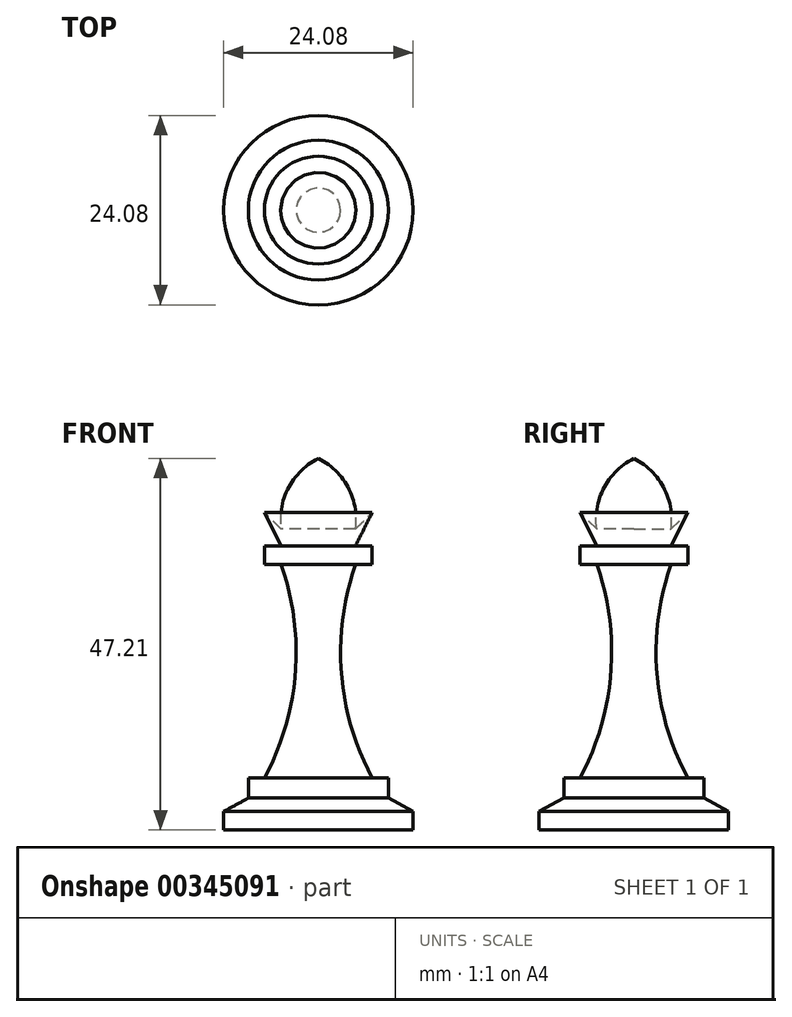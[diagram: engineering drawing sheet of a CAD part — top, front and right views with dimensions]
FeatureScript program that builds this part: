
annotation { "Feature Type Name" : "Feature", "Feature Type Description" : "" }
export const myFeature = defineFeature(function(context is Context, id is Id, definition is map)
    precondition{}
    {
        {
            var Q0;
            Q0=qCreatedBy(makeId("Front.planeOp"),FACE);
            var sketch = newSketch(context, id + "F0", { "sketchPlane" : qUnion([Q0])});
            skLineSegment(sketch, "E0", {"start": v(4.72, 27.14) * mm, "end": v(6.84, 27.14) * mm});
            skLineSegment(sketch, "E1", {"start": v(6.84, 27.14) * mm, "end": v(6.84, 29.5) * mm});
            skLineSegment(sketch, "E2", {"start": v(6.84, 29.5) * mm, "end": v(4.72, 29.5) * mm});
            skLineSegment(sketch, "E3", {"start": v(4.72, 29.5) * mm, "end": v(6.84, 33.75) * mm});
            skLineSegment(sketch, "E4", {"start": v(6.84, 33.75) * mm, "end": v(4.72, 31.63) * mm});
            skArc(sketch, "E5", {"start": v(4.72, 31.63) * mm, "mid": v(3.8, 36.87) * mm, "end": v(0, 40.6) * mm});
            skLineSegment(sketch, "E6", {"start": v(0, 40.6) * mm, "end": v(0, 0) * mm});
            skLineSegment(sketch, "E7", {"start": v(0, 0) * mm, "end": v(6.84, 0) * mm});
            skArc(sketch, "E8", {"start": v(4.72, 27.14) * mm, "mid": v(2.92, 13.35) * mm, "end": v(6.84, 0) * mm});
            skSolve(sketch);
        }
        {
            var Q0;
            Q0 = qSketchRegion(id + "F0", true);
            var Q1;
            Q1=sQuery(id+"F0.wireOp",EDGE,"E6");
            revolve(context, id + "F1", {"entities" : qUnion([Q0]), "axis" : qUnion([Q1]), "revolveType" : RevolveType.FULL});
        }
        {
            var Q0;
            Q0=qCreatedBy(makeId("Front.planeOp"),FACE);
            var sketch = newSketch(context, id + "F2", { "sketchPlane" : qUnion([Q0])});
            skLineSegment(sketch, "E9", {"start": v(0, 0) * mm, "end": v(8.9, 0) * mm});
            skLineSegment(sketch, "E10", {"start": v(8.9, 0) * mm, "end": v(8.9, -2.54) * mm});
            skLineSegment(sketch, "E11", {"start": v(0, -2.54) * mm, "end": v(0, 0) * mm});
            skLineSegment(sketch, "E12", {"start": v(8.9, -2.54) * mm, "end": v(12.04, -4.25) * mm});
            skLineSegment(sketch, "E13", {"start": v(12.04, -4.25) * mm, "end": v(12.04, -6.6) * mm});
            skLineSegment(sketch, "E14", {"start": v(12.04, -6.6) * mm, "end": v(0, -6.6) * mm});
            skLineSegment(sketch, "E15", {"start": v(0, -6.6) * mm, "end": v(0, 0) * mm});
            skSolve(sketch);
        }
        {
            var Q0;
            Q0 = qSketchRegion(id + "F2", true);
            var Q1;
            Q1=sQuery(id+"F2.wireOp",EDGE,"E11");
            revolve(context, id + "F3", {"operationType" : NewBodyOperationType.ADD, "entities" : qUnion([Q0]), "axis" : qUnion([Q1]), "revolveType" : RevolveType.FULL});
        }
    });
